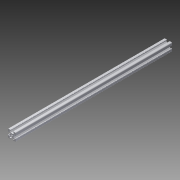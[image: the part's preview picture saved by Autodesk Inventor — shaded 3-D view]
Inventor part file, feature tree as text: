
AUTODESK INVENTOR PART (.ipt)
format: ipt  version: 2015 SP1 (Build 190203100, 203)  size: 151,040 bytes
history: native  units: mm
features: extrude x2, mirror x2, sketch x2, fillet x1
ambient origin geometry x8: Origin, YZ Plane, XZ Plane, XY Plane, X Axis, Y Axis, Z Axis, Center Point
bodies: Solid1 (feature_tree)
feature tree (7):
  extrude  "Extrusion1"  Depth=10.0mm
  fillet  "Fillet1"  Radius=10.0mm
  mirror  "Mirror1"
  mirror  "Mirror2"
  extrude  "Extrusion2"  Depth=6.1mm
  sketch  "Sketch1"  dims[d0=45.0deg d1=5.63mm d2=10.0mm]
  sketch  "Sketch2"  dims[d3=3.1mm d5=6.1mm d6=1.5mm d7=2.0mm d8=400.0mm d9=0.0mm d10=1.5mm d11=3.6mm d12=4.45mm d13=10.0mm d14=0.0mm]
